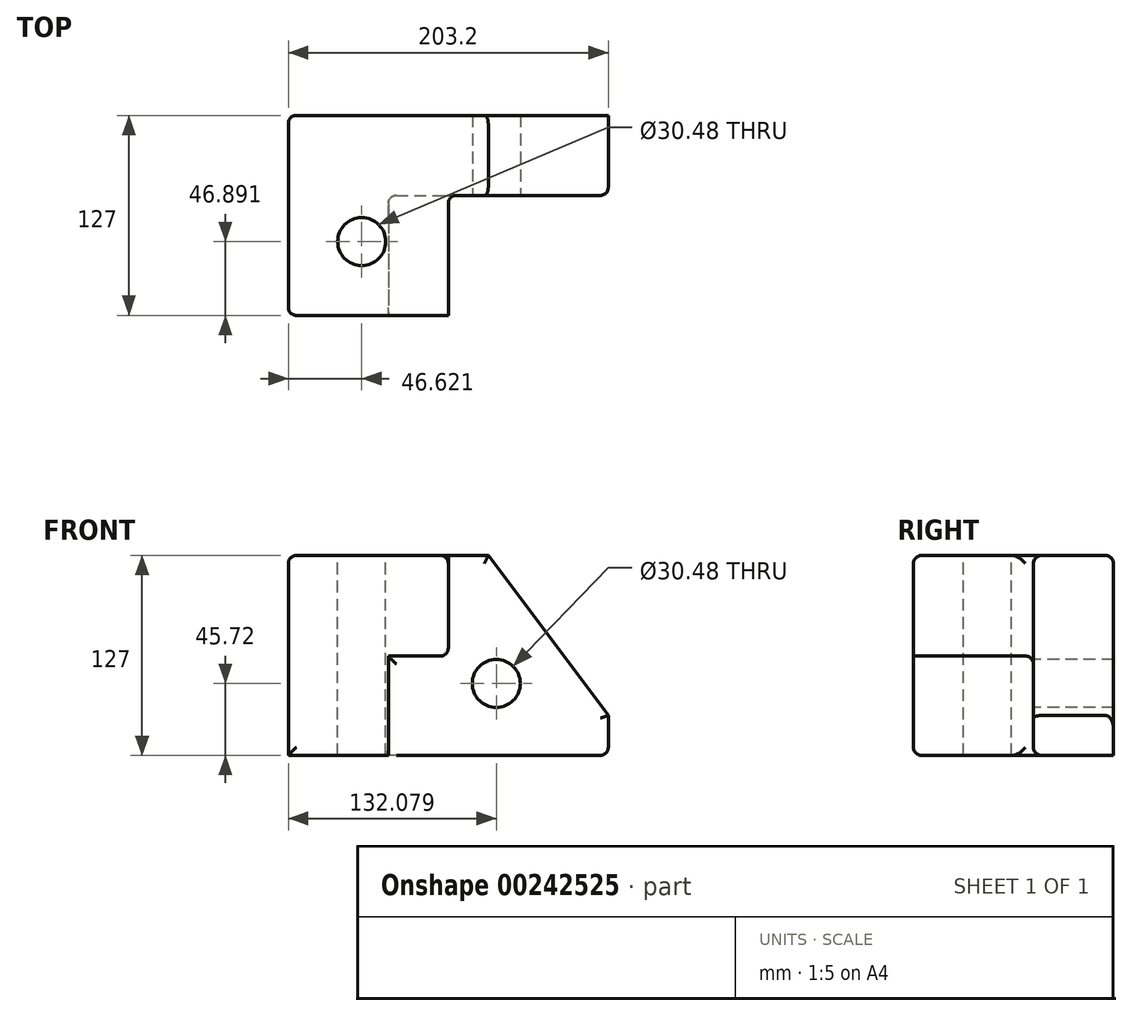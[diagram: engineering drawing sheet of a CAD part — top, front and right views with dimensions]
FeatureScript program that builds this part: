
annotation { "Feature Type Name" : "Feature", "Feature Type Description" : "" }
export const myFeature = defineFeature(function(context is Context, id is Id, definition is map)
    precondition{}
    {
        {
            var Q0;
            Q0=qCreatedBy(makeId("Front.planeOp"),FACE);
            var sketch = newSketch(context, id + "F0", { "sketchPlane" : qUnion([Q0])});
            skLineSegment(sketch, "E0.bottom", {"start": v(-102.9, -63.13) * mm, "end": v(100.3, -63.13) * mm});
            skLineSegment(sketch, "E0.top", {"start": v(-102.9, 63.87) * mm, "end": v(100.3, 63.87) * mm});
            skLineSegment(sketch, "E0.left", {"start": v(-102.9, -63.13) * mm, "end": v(-102.9, 63.87) * mm});
            skLineSegment(sketch, "E0.right", {"start": v(100.3, -63.13) * mm, "end": v(100.3, 63.87) * mm});
            skSolve(sketch);
        }
        {
            var Q0;
            Q0 = qSketchRegion(id + "F0", true);
            extrude(context, id + "F1", {"entities" : qUnion([Q0]), "depth" : 127 * mm});
        }
        {
            var Q0;
            Q0=makeQuery(id+"F1.opExtrude","CAP_FACE",FACE,{"disambiguationData":[OSD([sQuery(id+"F0.wireOp",EDGE,"E0.bottom"),sQuery(id+"F0.wireOp",EDGE,"E0.top"),sQuery(id+"F0.wireOp",EDGE,"E0.left"),sQuery(id+"F0.wireOp",EDGE,"E0.right")])],"isStart":false});
            var sketch = newSketch(context, id + "F2", { "sketchPlane" : qUnion([Q0])});
            skLineSegment(sketch, "E1", {"start": v(-102.9, -63.13) * mm, "end": v(-39.4, -63.13) * mm});
            skLineSegment(sketch, "E2", {"start": v(-39.4, -63.13) * mm, "end": v(-39.4, 0) * mm});
            skLineSegment(sketch, "E3", {"start": v(-39.4, 0) * mm, "end": v(-1.3, 0) * mm});
            skLineSegment(sketch, "E4", {"start": v(-1.3, 0) * mm, "end": v(-1.3, 63.87) * mm});
            skSolve(sketch);
        }
        {
            var Q0;
            {var subQ2=sQuery(id+"F2.wireOp",EDGE,"E2");Q0=makeQuery(id+"F2.imprint","IMPRINT",FACE,{"disambiguationData":[TD([[makeQuery(id+"F2.imprint","IMPRINT",EDGE,{"derivedFrom":subQ2}),-1.0]])]});}
            extrude(context, id + "F3", {"entities" : qUnion([Q0]), "operationType" : NewBodyOperationType.REMOVE, "oppositeDirection" : true, "depth" : 76.2 * mm});
        }
        {
            var Q0;
            Q0=makeQuery(id+"F1.opExtrude","SWEPT_EDGE",EDGE,{"disambiguationData":[OSD([sQuery(id+"F0.wireOp",EDGE,"E0.top"),sQuery(id+"F0.wireOp",EDGE,"E0.right")])]});
            chamfer(context, id + "F4", {"entities" : qUnion([Q0]), "chamferType" : ChamferType.TWO_OFFSETS, "width1" : 76.2 * mm, "oppositeDirection" : false, "width2" : 101.6 * mm, "tangentPropagation" : true});
        }
        {
            var Q0;
            Q0=makeQuery(id+"F3.boolean.opBoolean","COPY",EDGE,{"derivedFrom":makeQuery(id+"F3.opExtrude","CAP_EDGE",EDGE,{"disambiguationData":[OSD([sQuery(id+"F0.wireOp",EDGE,"E0.top")])],"isStart":false})});
            var Q1;
            Q1=makeQuery(id+"F3.boolean.opBoolean","COPY",EDGE,{"derivedFrom":makeQuery(id+"F3.opExtrude","SWEPT_EDGE",EDGE,{"disambiguationData":[OSD([sQuery(id+"F0.wireOp",EDGE,"E0.top"),sQuery(id+"F2.wireOp",EDGE,"E4")])]})});
            var Q2;
            Q2=makeQuery(id+"F1.opExtrude","CAP_EDGE",EDGE,{"disambiguationData":[OSD([sQuery(id+"F0.wireOp",EDGE,"E0.top")])],"isStart":false});
            var Q3;
            Q3=makeQuery(id+"F3.boolean.opBoolean","COPY",FACE,{"derivedFrom":makeQuery(id+"F3.opExtrude","CAP_FACE",FACE,{"disambiguationData":[OSD([sQuery(id+"F0.wireOp",EDGE,"E0.bottom"),sQuery(id+"F0.wireOp",EDGE,"E0.top"),sQuery(id+"F0.wireOp",EDGE,"E0.right"),sQuery(id+"F2.wireOp",EDGE,"E2"),sQuery(id+"F2.wireOp",EDGE,"E3"),sQuery(id+"F2.wireOp",EDGE,"E4")])],"isStart":false})});
            var Q4;
            Q4=makeQuery(id+"F3.boolean.opBoolean","COPY",EDGE,{"derivedFrom":makeQuery(id+"F3.opExtrude","CAP_EDGE",EDGE,{"disambiguationData":[OSD([sQuery(id+"F2.wireOp",EDGE,"E4")])],"isStart":true})});
            var Q5;
            Q5=makeQuery(id+"F3.boolean.opBoolean","COPY",EDGE,{"derivedFrom":makeQuery(id+"F3.opExtrude","SWEPT_EDGE",EDGE,{"disambiguationData":[OSD([sQuery(id+"F2.wireOp",EDGE,"E3"),sQuery(id+"F2.wireOp",EDGE,"E4")])]})});
            var Q6;
            Q6=makeQuery(id+"F3.boolean.opBoolean","COPY",EDGE,{"derivedFrom":makeQuery(id+"F3.opExtrude","CAP_EDGE",EDGE,{"disambiguationData":[OSD([sQuery(id+"F2.wireOp",EDGE,"E2")])],"isStart":true})});
            var Q7;
            Q7=makeQuery(id+"F1.opExtrude","SWEPT_EDGE",EDGE,{"disambiguationData":[OSD([sQuery(id+"F0.wireOp",EDGE,"E0.bottom"),sQuery(id+"F0.wireOp",EDGE,"E0.right")])]});
            var Q8;
            Q8=makeQuery(id+"F1.opExtrude","CAP_EDGE",EDGE,{"disambiguationData":[OSD([sQuery(id+"F0.wireOp",EDGE,"E0.bottom")])],"isStart":false});
            var Q9;
            Q9=makeQuery(id+"F1.opExtrude","CAP_EDGE",EDGE,{"disambiguationData":[OSD([sQuery(id+"F0.wireOp",EDGE,"E0.top")])],"isStart":true});
            var Q10;
            {var subQ0=sQuery(id+"F0.wireOp",EDGE,"E0.right");var subQ1=sQuery(id+"F0.wireOp",EDGE,"E0.top");Q10=makeQuery(id+"F4.opChamfer","BLEND_EDGE",EDGE,{"blendedFrom":[makeQuery(id+"F1.opExtrude","SWEPT_EDGE",EDGE,{"disambiguationData":[OSD([subQ1,subQ0])]}),makeQuery(id+"F1.opExtrude","CAP_FACE",FACE,{"disambiguationData":[OSD([sQuery(id+"F0.wireOp",EDGE,"E0.bottom"),subQ1,sQuery(id+"F0.wireOp",EDGE,"E0.left"),subQ0])],"isStart":true})],"blendedInto":[makeQuery(id+"F1.opExtrude","CAP_FACE",FACE,{"disambiguationData":[OSD([sQuery(id+"F0.wireOp",EDGE,"E0.bottom"),subQ1,sQuery(id+"F0.wireOp",EDGE,"E0.left"),subQ0])],"isStart":true})]});}
            var Q11;
            Q11=makeQuery(id+"F1.opExtrude","SWEPT_EDGE",EDGE,{"disambiguationData":[OSD([sQuery(id+"F0.wireOp",EDGE,"E0.top"),sQuery(id+"F0.wireOp",EDGE,"E0.left")])]});
            var Q12;
            Q12=makeQuery(id+"F1.opExtrude","CAP_EDGE",EDGE,{"disambiguationData":[OSD([sQuery(id+"F0.wireOp",EDGE,"E0.left")])],"isStart":false});
            var Q13;
            Q13=makeQuery(id+"F1.opExtrude","CAP_EDGE",EDGE,{"disambiguationData":[OSD([sQuery(id+"F0.wireOp",EDGE,"E0.left")])],"isStart":true});
            fillet(context, id + "F5", {"entities" : qUnion([Q0, Q1, Q2, Q3, Q4, Q5, Q6, Q7, Q8, Q9, Q10, Q11, Q12, Q13]), "radius" : 5.08 * mm, "tangentPropagation" : true, "allowEdgeOverflow" : false});
        }
        {
            var Q0;
            Q0=makeQuery(id+"F3.boolean.opBoolean","COPY",FACE,{"derivedFrom":makeQuery(id+"F3.opExtrude","CAP_FACE",FACE,{"disambiguationData":[OSD([sQuery(id+"F0.wireOp",EDGE,"E0.bottom"),sQuery(id+"F0.wireOp",EDGE,"E0.top"),sQuery(id+"F0.wireOp",EDGE,"E0.right"),sQuery(id+"F2.wireOp",EDGE,"E2"),sQuery(id+"F2.wireOp",EDGE,"E3"),sQuery(id+"F2.wireOp",EDGE,"E4")])],"isStart":false})});
            var sketch = newSketch(context, id + "F6", { "sketchPlane" : qUnion([Q0])});
            skCircle(sketch, "E5", {"center": v(29.18, -17.4) * mm, "radius": 15.24 * mm});
            skSolve(sketch);
        }
        {
            var Q0;
            Q0=makeQuery(id+"F6.imprint","IMPRINT",FACE,{"disambiguationData":[TD([[makeQuery(id+"F6.imprint","IMPRINT",EDGE,{"derivedFrom":sQuery(id+"F6.wireOp",EDGE,"E5")}),1.0]])]});
            var Q1;
            Q1=makeQuery(id+"F1.opExtrude","CAP_FACE",FACE,{"disambiguationData":[OSD([sQuery(id+"F0.wireOp",EDGE,"E0.bottom"),sQuery(id+"F0.wireOp",EDGE,"E0.top"),sQuery(id+"F0.wireOp",EDGE,"E0.left"),sQuery(id+"F0.wireOp",EDGE,"E0.right")])],"isStart":true});
            extrude(context, id + "F7", {"entities" : qUnion([Q0]), "operationType" : NewBodyOperationType.REMOVE, "endBound" : BoundingType.UP_TO_SURFACE, "oppositeDirection" : true, "endBoundEntityFace" : qUnion([Q1]), "depth" : 122.17 * mm});
        }
        {
            var Q0;
            Q0=makeQuery(id+"F1.opExtrude","SWEPT_FACE",FACE,{"disambiguationData":[OSD([sQuery(id+"F0.wireOp",EDGE,"E0.top")])]});
            var sketch = newSketch(context, id + "F8", { "sketchPlane" : qUnion([Q0])});
            skCircle(sketch, "E6", {"center": v(-56.28, -80.1) * mm, "radius": 15.24 * mm});
            skSolve(sketch);
        }
        {
            var Q0;
            Q0=makeQuery(id+"F8.imprint","IMPRINT",FACE,{"disambiguationData":[TD([[makeQuery(id+"F8.imprint","IMPRINT",EDGE,{"derivedFrom":sQuery(id+"F8.wireOp",EDGE,"E6")}),1.0]])]});
            var Q1;
            Q1=makeQuery(id+"F1.opExtrude","SWEPT_FACE",FACE,{"disambiguationData":[OSD([sQuery(id+"F0.wireOp",EDGE,"E0.bottom")])]});
            extrude(context, id + "F9", {"entities" : qUnion([Q0]), "operationType" : NewBodyOperationType.REMOVE, "endBound" : BoundingType.UP_TO_SURFACE, "oppositeDirection" : true, "endBoundEntityFace" : qUnion([Q1]), "depth" : 25.4 * mm});
        }
    });
